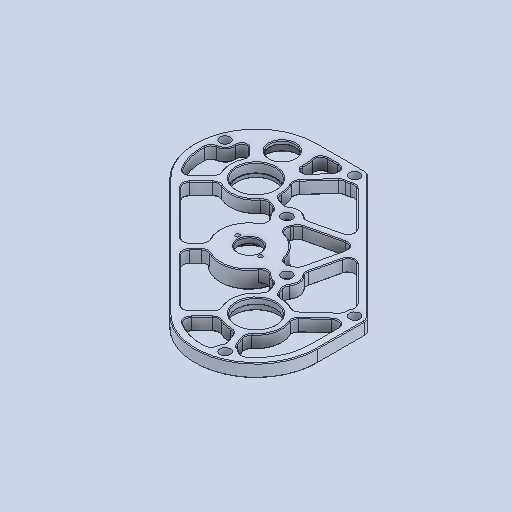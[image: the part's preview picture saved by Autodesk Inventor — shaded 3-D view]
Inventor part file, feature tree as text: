
AUTODESK INVENTOR PART (.ipt)
format: ipt  version: 2024.2 (Build 282272000, 272)  size: 486,400 bytes
history: native  units: in
note: dims shown in document units (in); Inventor stores cm internally (conversion verified against a paired STEP export)
features: chamfer x1
ambient origin geometry x8: Origin, YZ Plane, XZ Plane, XY Plane, X Axis, Y Axis, Z Axis, Center Point
bodies: Solid1 (feature_tree)
feature tree (1):
  chamfer  "Chamfer4"  [1 undecoded]
note: 1 required parameter value undecoded (feature->parameter linkage not recoverable at this tier; creation-order binding heuristic only, values carry confidence <= 0.55)
